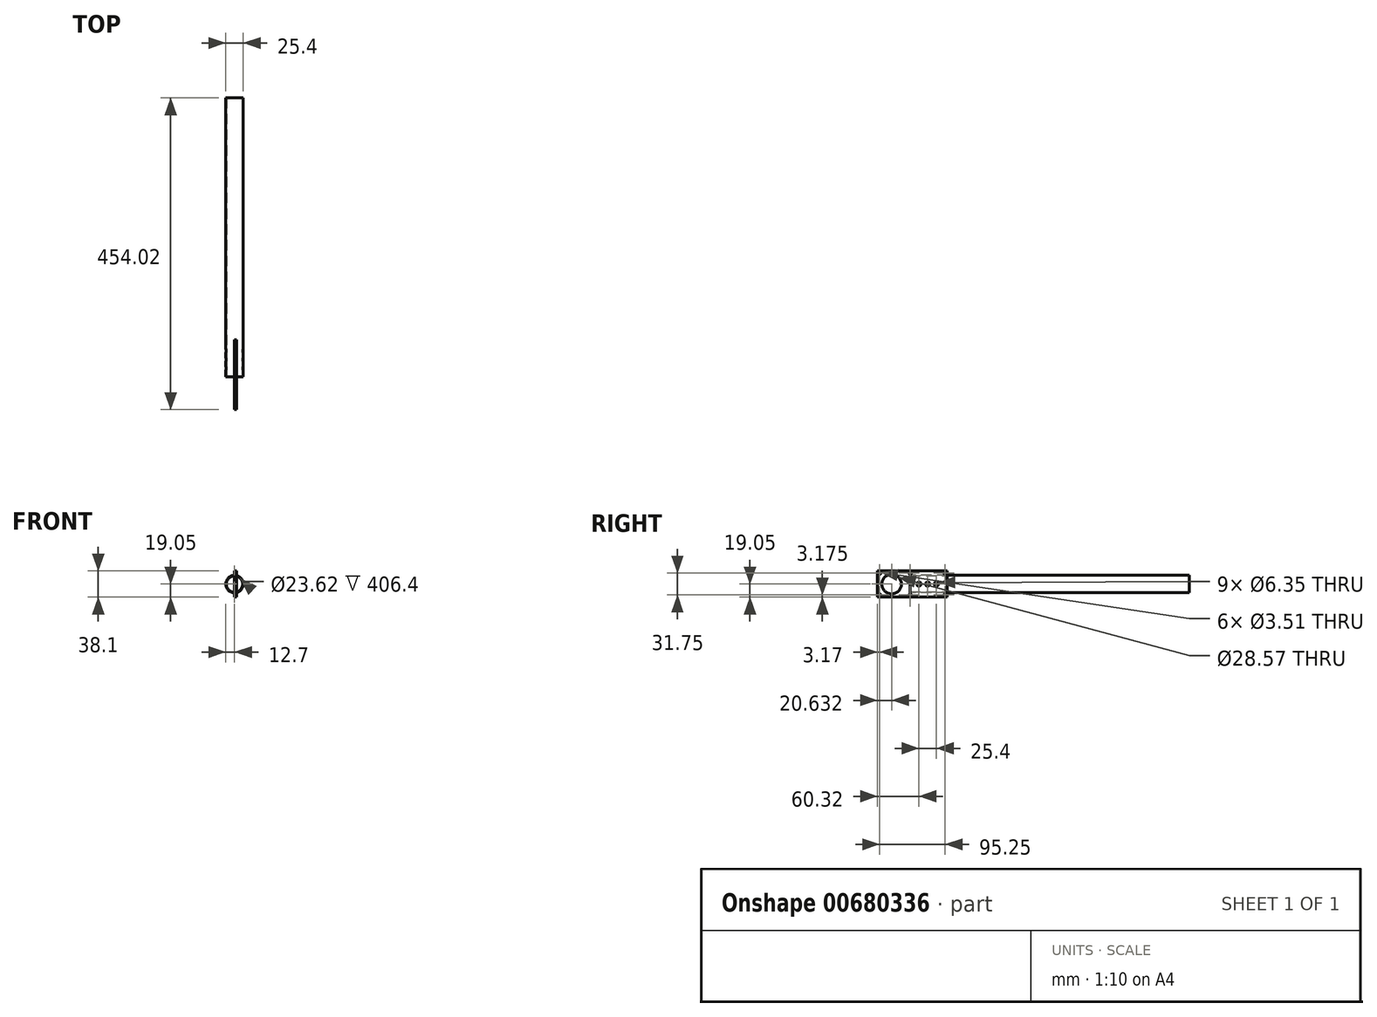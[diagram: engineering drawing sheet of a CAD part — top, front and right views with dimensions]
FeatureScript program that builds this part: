
annotation { "Feature Type Name" : "Feature", "Feature Type Description" : "" }
export const myFeature = defineFeature(function(context is Context, id is Id, definition is map)
    precondition{}
    {
        {
            var Q0;
            Q0=qCreatedBy(makeId("Front.planeOp"),FACE);
            var sketch = newSketch(context, id + "F0", { "sketchPlane" : qUnion([Q0])});
            skCircle(sketch, "E0", {"center": v(0, 0) * mm, "radius": 12.7 * mm});
            skCircle(sketch, "E1", {"center": v(0, 0) * mm, "radius": 11.81 * mm});
            skSolve(sketch);
        }
        {
            var Q0;
            Q0 = qSketchRegion(id + "F0", true);
            extrude(context, id + "F1", {"entities" : qUnion([Q0]), "oppositeDirection" : true, "depth" : 406.4 * mm, "offsetDistance" : 25.4 * mm});
        }
        {
            var Q0;
            Q0=qCreatedBy(makeId("Right.planeOp"),FACE);
            var sketch = newSketch(context, id + "F2", { "sketchPlane" : qUnion([Q0])});
            skLineSegment(sketch, "E2", {"start": v(0, 0) * mm, "end": v(91.96, 0) * mm, "construction": true});
            skCircle(sketch, "E3", {"center": v(12.7, 0) * mm, "radius": 3.18 * mm});
            skCircle(sketch, "E4", {"center": v(25.4, 0) * mm, "radius": 3.18 * mm});
            skCircle(sketch, "E5", {"center": v(38.1, 0) * mm, "radius": 3.18 * mm});
            skSolve(sketch);
        }
        {
            var Q0;
            Q0 = qSketchRegion(id + "F2", true);
            extrude(context, id + "F3", {"entities" : qUnion([Q0]), "operationType" : NewBodyOperationType.REMOVE, "endBound" : BoundingType.THROUGH_ALL, "depth" : 25.4 * mm, "offsetDistance" : 25.4 * mm, "hasSecondDirection" : true, "secondDirectionOppositeDirection" : true, "secondDirectionDepth" : 25.4 * mm});
        }
        {
            var Q0;
            Q0=qCreatedBy(makeId("Right.planeOp"),FACE);
            var sketch = newSketch(context, id + "F4", { "sketchPlane" : qUnion([Q0])});
            skLineSegment(sketch, "E6.bottom", {"start": v(-47.62, 19.05) * mm, "end": v(53.98, 19.05) * mm});
            skLineSegment(sketch, "E6.top", {"start": v(-47.62, -19.05) * mm, "end": v(53.98, -19.05) * mm});
            skLineSegment(sketch, "E6.left", {"start": v(-47.63, 19.05) * mm, "end": v(-47.62, -19.05) * mm});
            skLineSegment(sketch, "E6.right", {"start": v(53.97, 19.05) * mm, "end": v(53.98, -19.05) * mm});
            skPoint(sketch, "E7", {"position": v(-47.63, 0) * mm});
            skCircle(sketch, "E8", {"center": v(-26.99, 0) * mm, "radius": 14.29 * mm});
            skLineSegment(sketch, "E9", {"start": v(-47.63, 15.87) * mm, "end": v(53.97, 15.87) * mm, "construction": true});
            skLineSegment(sketch, "E10", {"start": v(25.4, 0) * mm, "end": v(25.4, 19.05) * mm, "construction": true});
            skCircle(sketch, "E11", {"center": v(50.8, 15.88) * mm, "radius": 1.75 * mm});
            skCircle(sketch, "E12.MirrorC", {"center": v(0, 15.88) * mm, "radius": 1.75 * mm});
            skCircle(sketch, "E13.MirrorC", {"center": v(0, -15.88) * mm, "radius": 1.75 * mm});
            skCircle(sketch, "E14.MirrorC", {"center": v(50.8, -15.88) * mm, "radius": 1.75 * mm});
            skCircle(sketch, "E15", {"center": v(12.7, 0) * mm, "radius": 3.18 * mm});
            skCircle(sketch, "E16", {"center": v(25.4, 0) * mm, "radius": 3.18 * mm});
            skCircle(sketch, "E17", {"center": v(38.1, 0) * mm, "radius": 3.18 * mm});
            skCircle(sketch, "E18", {"center": v(-44.45, 15.87) * mm, "radius": 1.75 * mm});
            skCircle(sketch, "E19.MirrorC", {"center": v(-44.45, -15.87) * mm, "radius": 1.75 * mm});
            skSolve(sketch);
        }
        {
            var Q0;
            Q0 = qSketchRegion(id + "F4", true);
            extrude(context, id + "F5", {"entities" : qUnion([Q0]), "depth" : 3.17 * mm, "offsetDistance" : 25.4 * mm});
        }
    });
